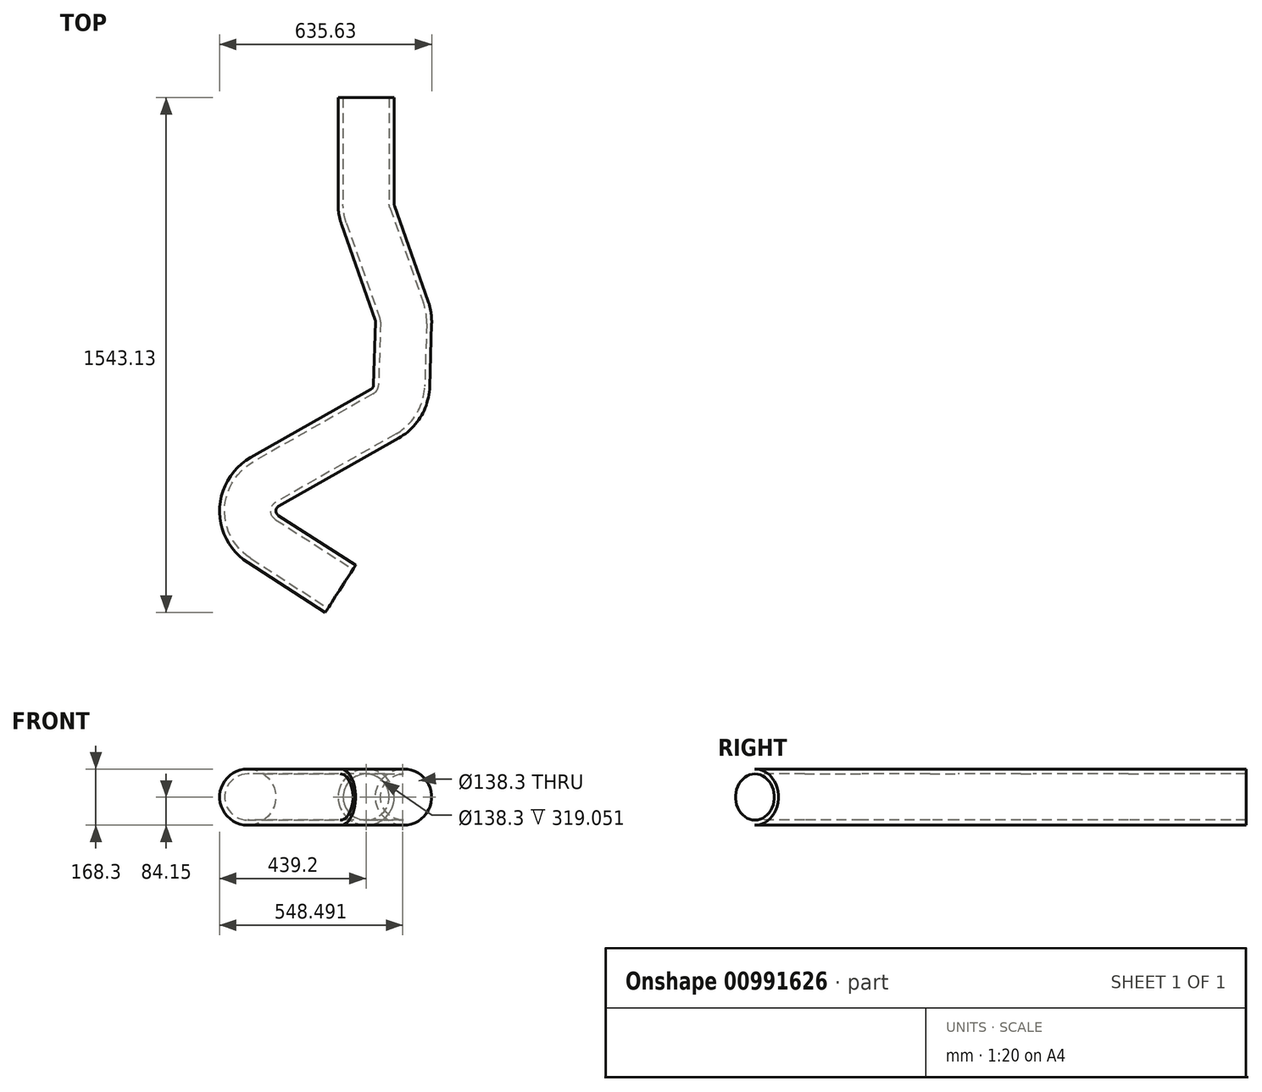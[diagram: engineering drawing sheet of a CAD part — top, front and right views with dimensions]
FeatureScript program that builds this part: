
annotation { "Feature Type Name" : "Feature", "Feature Type Description" : "" }
export const myFeature = defineFeature(function(context is Context, id is Id, definition is map)
    precondition{}
    {
        {
            var Q0;
            Q0=qCreatedBy(makeId("Front.planeOp"),FACE);
            var sketch = newSketch(context, id + "F0", { "sketchPlane" : qUnion([Q0])});
            skCircle(sketch, "E0", {"center": v(0, 0) * mm, "radius": 84.15 * mm});
            skCircle(sketch, "E1", {"center": v(0, 0) * mm, "radius": 69.15 * mm});
            skSolve(sketch);
        }
        {
            var Q0;
            Q0=qCreatedBy(makeId("Top.planeOp"),FACE);
            var sketch = newSketch(context, id + "F1", { "sketchPlane" : qUnion([Q0])});
            skLineSegment(sketch, "E2", {"start": v(0, 0) * mm, "end": v(0, -319.05) * mm});
            skLineSegment(sketch, "E3", {"start": v(5.68, -352.28) * mm, "end": v(106.6, -638.69) * mm});
            skLineSegment(sketch, "E4", {"start": v(112.24, -675.04) * mm, "end": v(106.35, -863.68) * mm});
            skLineSegment(sketch, "E5", {"start": v(55.79, -947.52) * mm, "end": v(-304.44, -1152.12) * mm});
            skLineSegment(sketch, "E6", {"start": v(-309.1, -1323.2) * mm, "end": v(-76.94, -1472.32) * mm});
            skPoint(sketch, "E7.visualSharp", {"position": v(0, -336.15) * mm});
            skArc(sketch, "E7.filletArc", {"start": v(0, -319.05) * mm, "mid": v(1.43, -335.9) * mm, "end": v(5.68, -352.28) * mm});
            skPoint(sketch, "E8.visualSharp", {"position": v(112.82, -656.34) * mm});
            skArc(sketch, "E8.filletArc", {"start": v(112.24, -675.04) * mm, "mid": v(111.1, -656.6) * mm, "end": v(106.6, -638.69) * mm});
            skPoint(sketch, "E9.visualSharp", {"position": v(104.6, -919.8) * mm});
            skArc(sketch, "E9.filletArc", {"start": v(55.79, -947.52) * mm, "mid": v(92.03, -912.2) * mm, "end": v(106.35, -863.68) * mm});
            skPoint(sketch, "E10.visualSharp", {"position": v(-448.27, -1233.81) * mm});
            skArc(sketch, "E10.filletArc", {"start": v(-304.44, -1152.12) * mm, "mid": v(-355.01, -1236.35) * mm, "end": v(-309.1, -1323.2) * mm});
            skSolve(sketch);
        }
        {
            var Q0;
            Q0=makeQuery(id+"F0.imprint","IMPRINT",FACE,{"disambiguationData":[TD([[makeQuery(id+"F0.imprint","IMPRINT",EDGE,{"derivedFrom":sQuery(id+"F0.wireOp",EDGE,"E0")}),1.0]])]});
            var Q1;
            Q1=sQuery(id+"F1.wireOp",EDGE,"E2");
            var Q2;
            Q2=sQuery(id+"F1.wireOp",EDGE,"E7.filletArc");
            var Q3;
            Q3=sQuery(id+"F1.wireOp",EDGE,"E4");
            var Q4;
            Q4=sQuery(id+"F1.wireOp",EDGE,"E8.filletArc");
            var Q5;
            Q5=sQuery(id+"F1.wireOp",EDGE,"E3");
            var Q6;
            Q6=sQuery(id+"F1.wireOp",EDGE,"E9.filletArc");
            var Q7;
            Q7=sQuery(id+"F1.wireOp",EDGE,"E5");
            var Q8;
            Q8=sQuery(id+"F1.wireOp",EDGE,"E10.filletArc");
            var Q9;
            Q9=sQuery(id+"F1.wireOp",EDGE,"E6");
            sweep(context, id + "F2", {"profiles" : qUnion([Q0]), "path" : qUnion([Q1, Q2, Q3, Q4, Q5, Q6, Q7, Q8, Q9])});
        }
    });
